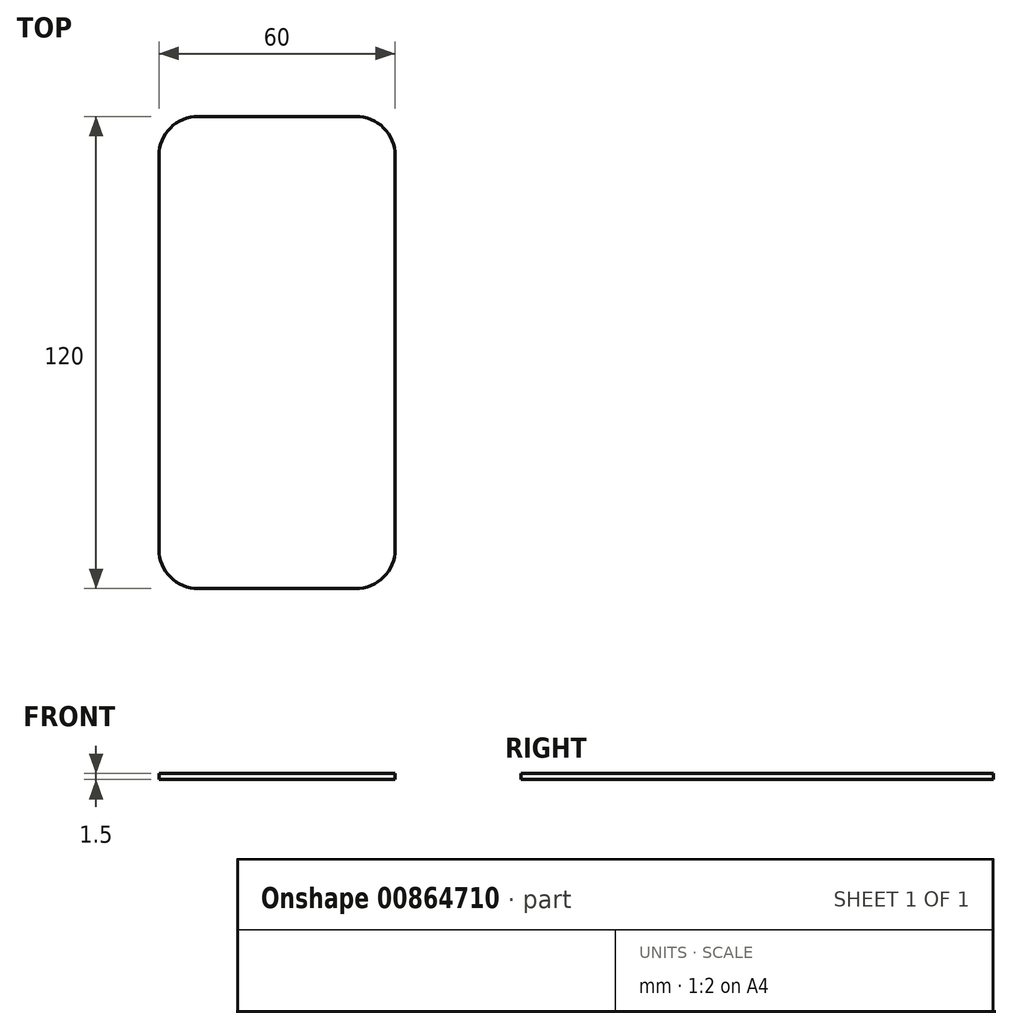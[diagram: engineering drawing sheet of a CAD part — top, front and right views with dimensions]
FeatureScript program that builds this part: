
annotation { "Feature Type Name" : "Feature", "Feature Type Description" : "" }
export const myFeature = defineFeature(function(context is Context, id is Id, definition is map)
    precondition{}
    {
        {
            var Q0;
            Q0=qCreatedBy(makeId("Top.planeOp"),FACE);
            var sketch = newSketch(context, id + "F0", { "sketchPlane" : qUnion([Q0])});
            skLineSegment(sketch, "E0.bottom", {"start": v(10, 0) * mm, "end": v(50, 0) * mm});
            skLineSegment(sketch, "E0.top", {"start": v(10, 120) * mm, "end": v(50, 120) * mm});
            skLineSegment(sketch, "E0.left", {"start": v(0, 10) * mm, "end": v(0, 110) * mm});
            skLineSegment(sketch, "E0.right", {"start": v(60, 10) * mm, "end": v(60, 110) * mm});
            skPoint(sketch, "E1.visualSharp", {"position": v(0, 120) * mm});
            skArc(sketch, "E1.filletArc", {"start": v(10, 120) * mm, "mid": v(2.93, 117.07) * mm, "end": v(0, 110) * mm});
            skPoint(sketch, "E2.visualSharp", {"position": v(60, 120) * mm});
            skArc(sketch, "E2.filletArc", {"start": v(60, 110) * mm, "mid": v(57.07, 117.07) * mm, "end": v(50, 120) * mm});
            skPoint(sketch, "E3.visualSharp", {"position": v(0, 0) * mm});
            skArc(sketch, "E3.filletArc", {"start": v(0, 10) * mm, "mid": v(2.93, 2.93) * mm, "end": v(10, 0) * mm});
            skPoint(sketch, "E4.visualSharp", {"position": v(60, 0) * mm});
            skArc(sketch, "E4.filletArc", {"start": v(50, 0) * mm, "mid": v(57.07, 2.93) * mm, "end": v(60, 10) * mm});
            skSolve(sketch);
        }
        {
            var Q0;
            Q0=makeQuery(id+"F0.imprint","IMPRINT",FACE,{"disambiguationData":[TD([[makeQuery(id+"F0.imprint","IMPRINT",EDGE,{"derivedFrom":sQuery(id+"F0.wireOp",EDGE,"E0.bottom")}),1.0]])]});
            extrude(context, id + "F1", {"entities" : qUnion([Q0]), "depth" : 1.5 * mm, "offsetDistance" : 25 * mm});
        }
    });
